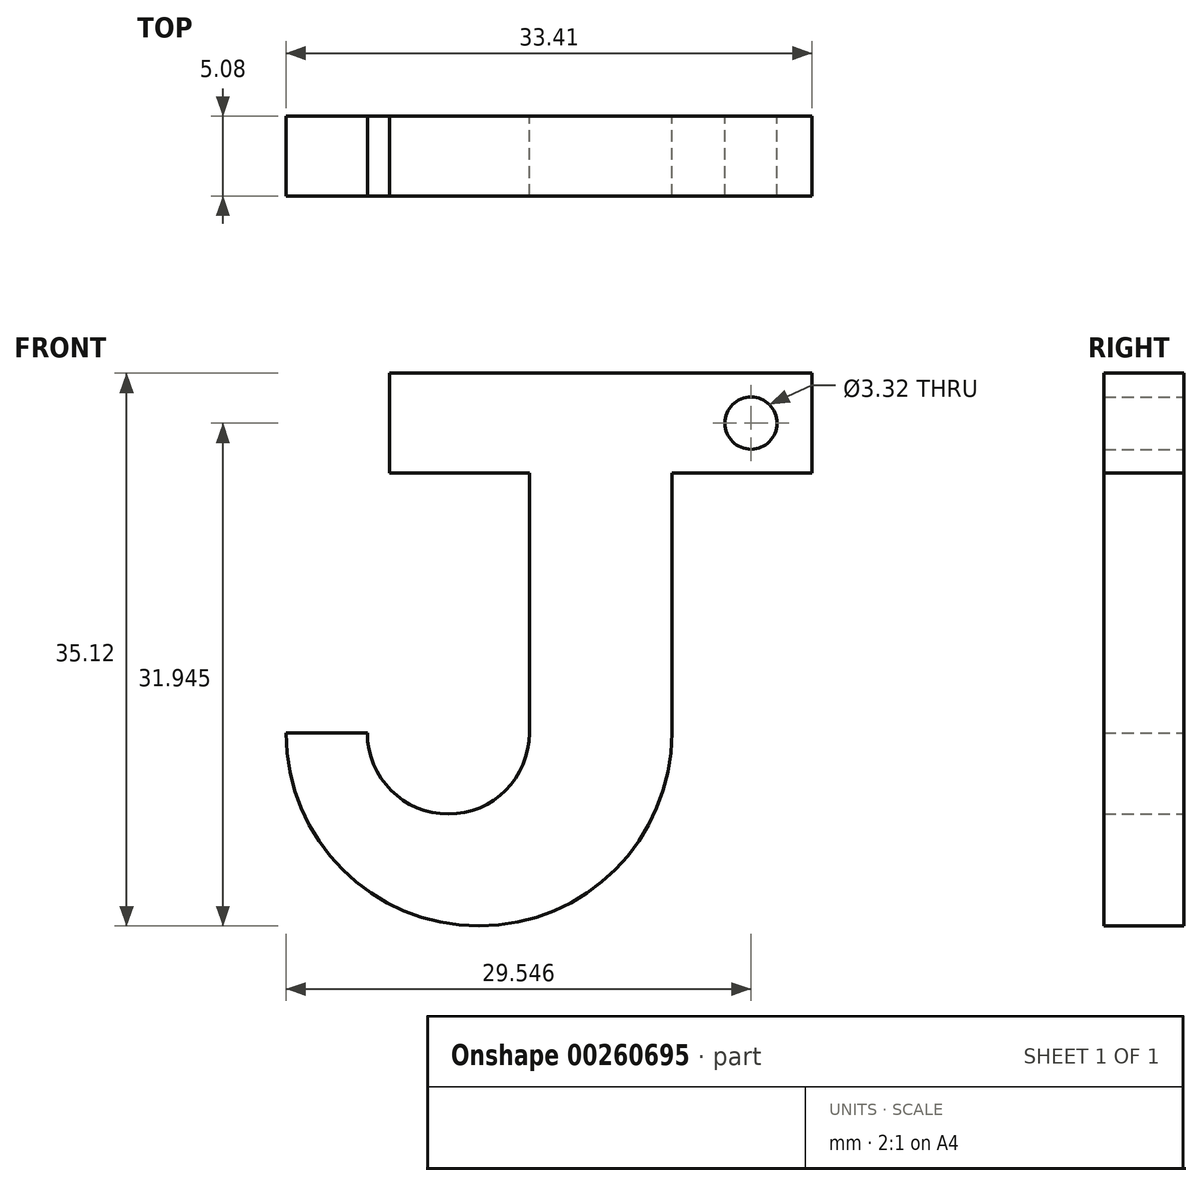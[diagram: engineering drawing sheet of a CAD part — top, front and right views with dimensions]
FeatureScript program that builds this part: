
annotation { "Feature Type Name" : "Feature", "Feature Type Description" : "" }
export const myFeature = defineFeature(function(context is Context, id is Id, definition is map)
    precondition{}
    {
        {
            var Q0;
            Q0=qCreatedBy(makeId("Front.planeOp"),FACE);
            var sketch = newSketch(context, id + "F0", { "sketchPlane" : qUnion([Q0])});
            skLineSegment(sketch, "E0", {"start": v(-20.64, 0) * mm, "end": v(22.86, 0) * mm});
            skLineSegment(sketch, "E1", {"start": v(-12.38, 31.75) * mm, "end": v(14.45, 31.75) * mm});
            skLineSegment(sketch, "E2", {"start": v(14.45, 31.75) * mm, "end": v(14.45, 25.4) * mm});
            skLineSegment(sketch, "E3", {"start": v(14.45, 25.4) * mm, "end": v(5.56, 25.4) * mm});
            skLineSegment(sketch, "E4", {"start": v(5.56, 25.4) * mm, "end": v(5.56, 8.89) * mm});
            skLineSegment(sketch, "E5", {"start": v(-12.38, 31.75) * mm, "end": v(-12.38, 25.4) * mm});
            skLineSegment(sketch, "E6", {"start": v(-12.38, 25.4) * mm, "end": v(-3.5, 25.4) * mm});
            skLineSegment(sketch, "E7", {"start": v(-3.5, 25.4) * mm, "end": v(-3.5, 8.89) * mm});
            skArc(sketch, "E8", {"start": v(-3.5, 8.89) * mm, "mid": v(-8.64, 3.74) * mm, "end": v(-13.79, 8.89) * mm});
            skLineSegment(sketch, "E9", {"start": v(-13.79, 8.89) * mm, "end": v(-18.96, 8.89) * mm});
            skArc(sketch, "E10", {"start": v(-18.96, 8.89) * mm, "mid": v(-6.7, -3.37) * mm, "end": v(5.56, 8.89) * mm});
            skCircle(sketch, "E11", {"center": v(10.59, 28.57) * mm, "radius": 1.66 * mm});
            skPoint(sketch, "E11.centerSnap0", {"position": v(14.45, 28.57) * mm});
            skSolve(sketch);
        }
        {
            var Q0;
            Q0=makeQuery(id+"F0.imprint","IMPRINT",FACE,{"disambiguationData":[TD([[makeQuery(id+"F0.imprint","IMPRINT",EDGE,{"derivedFrom":sQuery(id+"F0.wireOp",EDGE,"E1")}),-1.0]])]});
            extrude(context, id + "F1", {"entities" : qUnion([Q0]), "depth" : 5.08 * mm});
        }
        {
            var Q0;
            Q0 = qSketchRegion(id + "F0", true);
            extrude(context, id + "F2", {"entities" : qUnion([Q0]), "operationType" : NewBodyOperationType.ADD, "depth" : 5.08 * mm});
        }
    });
